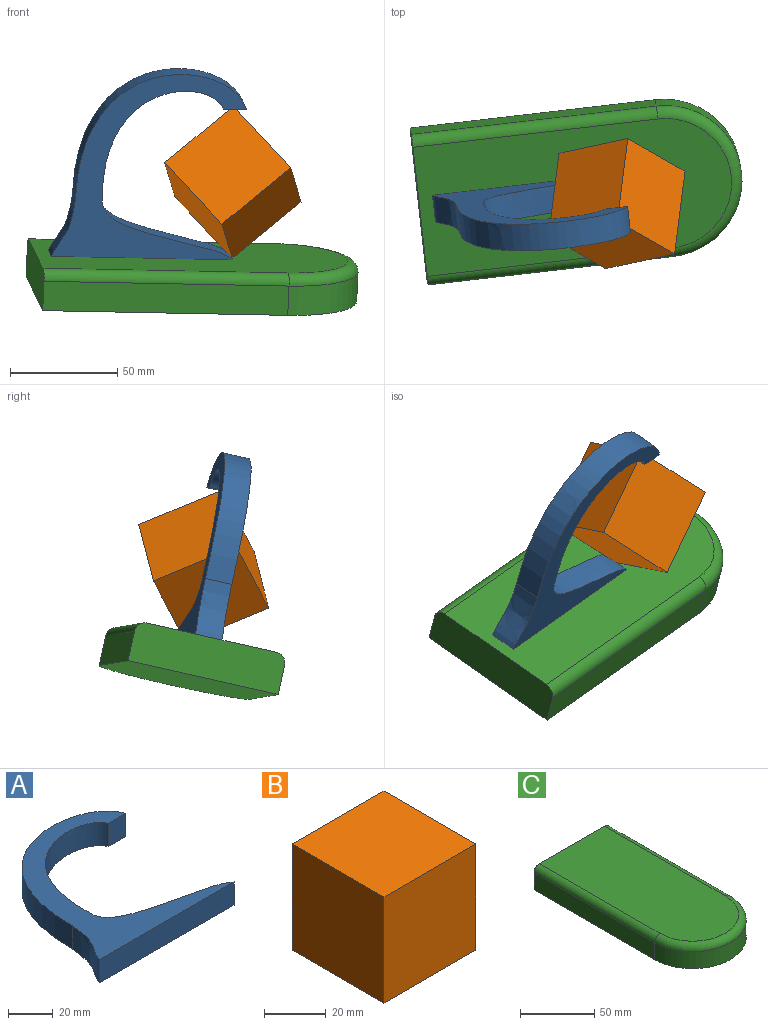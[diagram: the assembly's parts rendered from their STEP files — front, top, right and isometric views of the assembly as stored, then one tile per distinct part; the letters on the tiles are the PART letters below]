
ASSEMBLY  parts=3 mates=2
PART A: 8 faces, bbox 88.2x98.1x12.7 mm
  f0: extruded ~62.46x26.98mm, area 898.1mm2, adj f1,f5,f6,f7
  f1: extruded ~54.88x52.99mm, area 1186.4mm2, adj f0,f2,f6,f7
  f2: plane 12.7x10.91mm, normal (0,-1,0), area 138.5mm2, adj f1,f3,f6,f7
  f3: extruded ~78.21x60.94mm, area 1570.7mm2, adj f2,f4,f6,f7
  f4: extruded ~26.98x12.7mm, area 370.8mm2, adj f3,f5,f6,f7
  f5: plane 84.97x12.7mm, normal (0,-1,0), area 1079.2mm2, adj f0,f4,f6,f7
  f6: plane 98.12x88.19mm, normal (0,0,1), area 2168.9mm2, adj f0,f1,f2,f3,f4,f5
  f7: plane 98.12x88.19mm, normal (0,0,-1), area 2168.9mm2, adj f0,f1,f2,f3,f4,f5
PART B: 6 faces, bbox 41.9x41.9x41.9 mm
  f0: plane 41.91x41.91mm, normal (-1,0,0), area 1756.4mm2, adj f1,f3,f4,f5
  f1: plane 41.91x41.91mm, normal (0,-1,0), area 1756.4mm2, adj f0,f2,f4,f5
  f2: plane 41.91x41.91mm, normal (1,0,0), area 1756.4mm2, adj f1,f3,f4,f5
  f3: plane 41.91x41.91mm, normal (0,1,0), area 1756.4mm2, adj f0,f2,f4,f5
  f4: plane 41.91x41.91mm, normal (0,0,1), area 1756.4mm2, adj f0,f1,f2,f3
  f5: plane 41.91x41.91mm, normal (0,0,-1), area 1756.4mm2, adj f0,f1,f2,f3
PART C: 9 faces, bbox 77.9x153.7x19.1 mm
  f0: plane 114.76x13.97mm, normal (-1,0,0), area 1603.2mm2, adj f1,f3,f5,f6
  f1: cylinder r=36.01mm len=72.01mm, axis (0,0,-1), area 1580.2mm2, adj f0,f2,f5,f7
  f2: plane 114.76x13.97mm, normal (1,0,0), area 1603.2mm2, adj f1,f3,f5,f8
  f3: plane 72.01x19.05mm, normal (0,1,0), area 1360.8mm2, adj f0,f2,f4,f5,f6,f8
  f4: plane 145.69x61.85mm, normal (0,0,1), area 8600.5mm2, adj f3,f6,f7,f8
  f5: plane 150.77x72.01mm, normal (0,0,-1), area 10300.6mm2, adj f0,f1,f2,f3
  f6: cylinder r=5.08mm len=114.76mm, axis (0,1,0), area 915.8mm2, adj f0,f3,f4,f7
  f7: torus R=30.93mm, axis (0,0,1), area 856.4mm2, adj f1,f4,f6,f8
  f8: cylinder r=5.08mm len=114.76mm, axis (0,-1,0), area 915.8mm2, adj f2,f3,f4,f7
PLACE A rot(axis=(1,0.07,0.04),102.8deg) t=(-35.79,-41.56,286.29)mm
PLACE B rot(axis=(-0.01,0.98,-0.22),139.8deg) t=(1.18,-32.88,292.72)mm
PLACE C rot(axis=(0.12,-0.09,0.99),97.1deg) t=(-20.84,-33.56,225.55)mm
MATE fastened A.f5 <-> C.f4  axis (-0.04,0.22,-0.98) through (-71.23,-36.55,246.68)mm
MATE ball A.f2 <-> B.f5  axis (-0.04,0.22,-0.98) through (14.78,-48.69,313.78)mm
